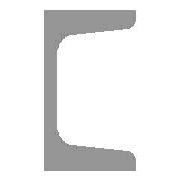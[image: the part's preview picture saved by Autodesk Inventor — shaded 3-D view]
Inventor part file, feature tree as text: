
AUTODESK INVENTOR PART (.ipt)
format: ipt  version: 2025 (Build 290162010, 162A)  size: 138,752 bytes
history: native  units: mm (DEFAULTED — no unit token found)
features: other x3, sketch x1, plane x1
ambient origin geometry x8: Origin, YZ Plane, XZ Plane, XY Plane, X Axis, Y Axis, Z Axis, Center Point
bodies: Solid1 (feature_tree), Body (feature_tree)
feature tree (5):
  other  "Driven Length"
  other  "Start plane"
  other  "End plane"
  sketch  "Sketch3"  dims[d0=5.0mm d1=50.0mm d2=50.0mm d3=7.5mm d4=22.5mm d5=1.968525mm d6=1500.0mm d7=0.0mm d23=8.0mm d24=4.0mm d25=15.4mm d26=-0.0mm d27=1500.0mm d28=90.0deg d29=1500.0mm]
  plane  "Work Plane3"
